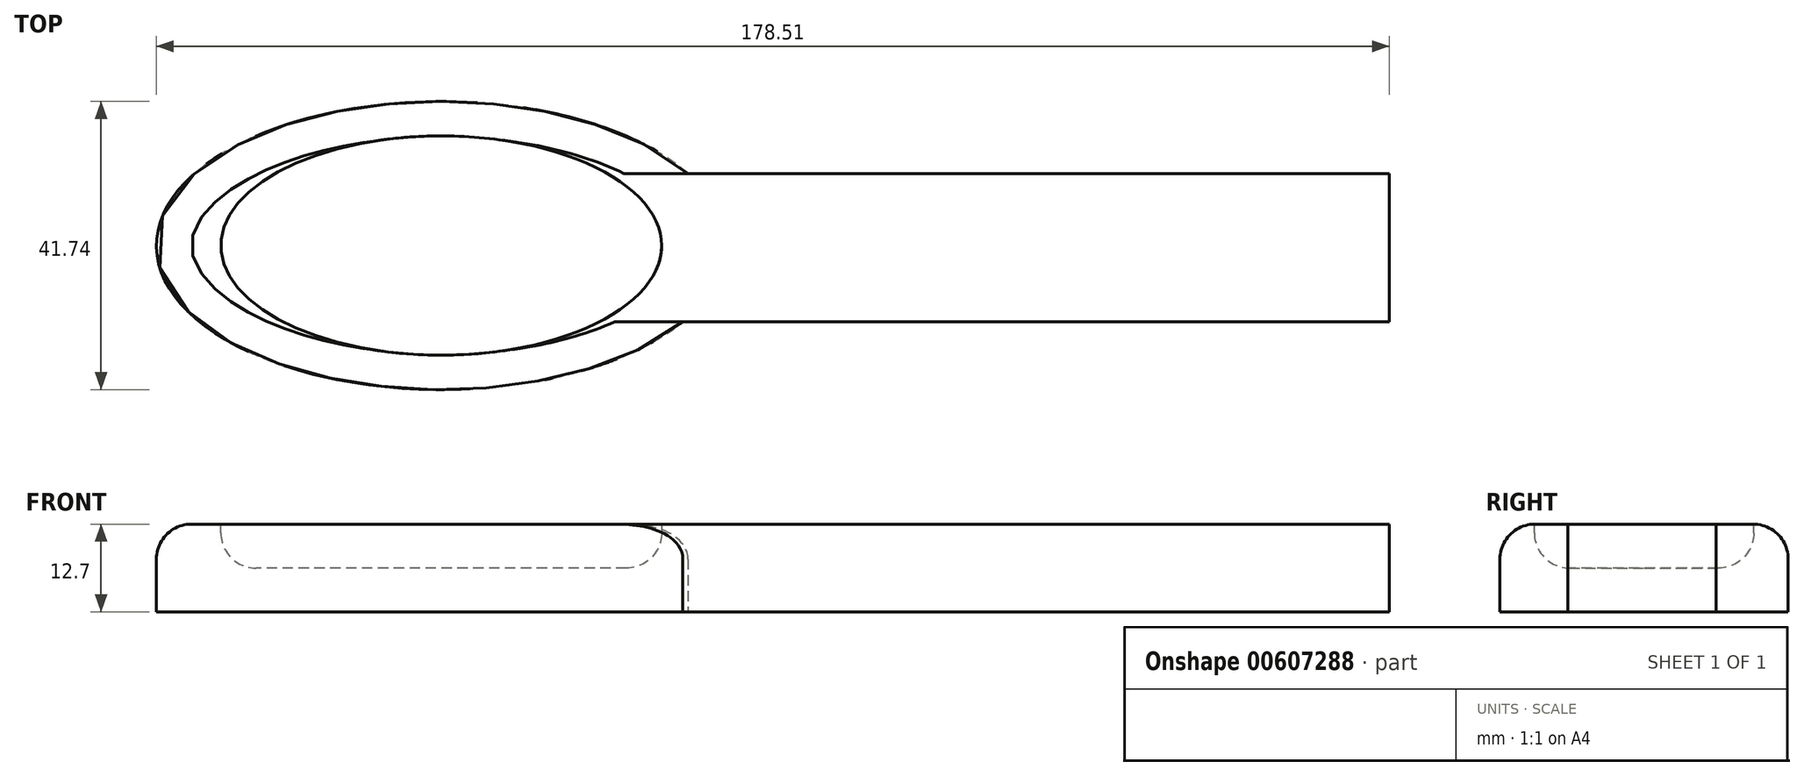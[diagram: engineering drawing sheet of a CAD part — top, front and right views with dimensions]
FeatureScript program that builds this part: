
annotation { "Feature Type Name" : "Feature", "Feature Type Description" : "" }
export const myFeature = defineFeature(function(context is Context, id is Id, definition is map)
    precondition{}
    {
        {
            var Q0;
            Q0=qCreatedBy(makeId("Top.planeOp"),FACE);
            var sketch = newSketch(context, id + "F0", { "sketchPlane" : qUnion([Q0])});
            skEllipse(sketch, "E0", {"center": v(-42.49, 0) * mm, "majorRadius": 41.25 * mm, "minorRadius": 20.87 * mm, "majorAxis": v(-1, 0)});
            skLineSegment(sketch, "E1", {"start": v(-6.75, 10.43) * mm, "end": v(94.78, 10.43) * mm});
            skLineSegment(sketch, "E2", {"start": v(94.78, 10.43) * mm, "end": v(94.78, 0) * mm});
            skLineSegment(sketch, "E3", {"start": v(94.78, 0) * mm, "end": v(94.78, -11.06) * mm});
            skLineSegment(sketch, "E4", {"start": v(94.78, -11.06) * mm, "end": v(-7.5, -11.06) * mm});
            skSolve(sketch);
        }
        {
            var Q0;
            Q0 = qSketchRegion(id + "F0", true);
            extrude(context, id + "F1", {"entities" : qUnion([Q0]), "depth" : 12.7 * mm, "offsetDistance" : 25.4 * mm});
        }
        {
            var Q0;
            Q0=makeQuery(id+"F1.opExtrude","CAP_FACE",FACE,{"disambiguationData":[OSD([sQuery(id+"F0.wireOp",EDGE,"E0"),sQuery(id+"F0.wireOp",EDGE,"E1"),sQuery(id+"F0.wireOp",EDGE,"E2"),sQuery(id+"F0.wireOp",EDGE,"E3"),sQuery(id+"F0.wireOp",EDGE,"E4")])],"isStart":false});
            var sketch = newSketch(context, id + "F2", { "sketchPlane" : qUnion([Q0])});
            skEllipse(sketch, "E5", {"center": v(-42.49, 0) * mm, "majorRadius": 31.9 * mm, "minorRadius": 15.88 * mm, "majorAxis": v(1, 0)});
            skSolve(sketch);
        }
        {
            var Q0;
            Q0 = qSketchRegion(id + "F2", true);
            extrude(context, id + "F3", {"entities" : qUnion([Q0]), "operationType" : NewBodyOperationType.REMOVE, "endBound" : BoundingType.SYMMETRIC, "depth" : 12.7 * mm, "offsetDistance" : 25.4 * mm});
        }
        {
            var Q0;
            Q0=makeQuery(id+"F7QX7uNN5bxrcsm_1.opFillet","SPLIT",FACE,{"disambiguationData":[OD(1.0)],"derivedFrom":makeQuery(id+"F1.opExtrude","CAP_FACE",FACE,{"disambiguationData":[OSD([sQuery(id+"F0.wireOp",EDGE,"E0"),sQuery(id+"F0.wireOp",EDGE,"E1"),sQuery(id+"F0.wireOp",EDGE,"E2"),sQuery(id+"F0.wireOp",EDGE,"E3"),sQuery(id+"F0.wireOp",EDGE,"E4")])],"isStart":false})});
            extrude(context, id + "F4", {"entities" : qUnion([Q0]), "operationType" : NewBodyOperationType.ADD, "oppositeDirection" : true, "depth" : 11.18 * mm, "offsetDistance" : 25.4 * mm});
        }
        {
            var Q0;
            Q0=makeQuery(id+"F1.opExtrude","CAP_EDGE",EDGE,{"disambiguationData":[OSD([sQuery(id+"F0.wireOp",EDGE,"E0")])],"isStart":false});
            var Q1;
            Q1=makeQuery(id+"F3.boolean.opBoolean","COPY",EDGE,{"derivedFrom":makeQuery(id+"F3.opExtrude","CAP_EDGE",EDGE,{"disambiguationData":[OSD([sQuery(id+"F2.wireOp",EDGE,"E5")])],"isStart":true})});
            fillet(context, id + "F5", {"entities" : qUnion([Q0, Q1]), "radius" : 5.08 * mm, "tangentPropagation" : true, "allowEdgeOverflow" : false});
        }
    });
